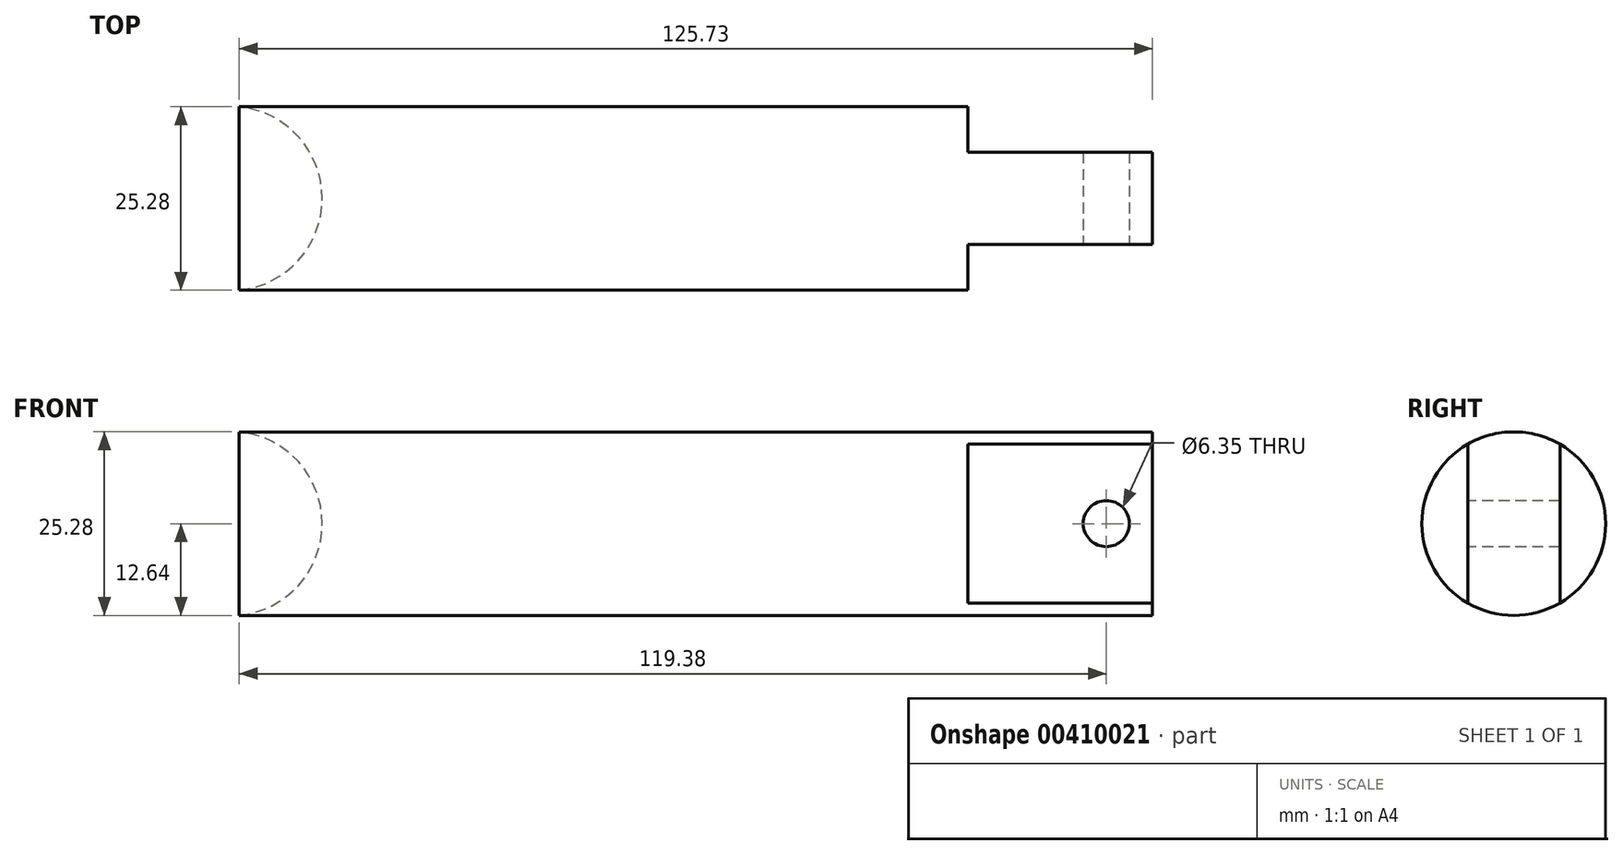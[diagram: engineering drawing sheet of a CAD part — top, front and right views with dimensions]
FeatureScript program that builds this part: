
annotation { "Feature Type Name" : "Feature", "Feature Type Description" : "" }
export const myFeature = defineFeature(function(context is Context, id is Id, definition is map)
    precondition{}
    {
        {
            var Q0;
            Q0=qCreatedBy(makeId("Front.planeOp"),FACE);
            var sketch = newSketch(context, id + "F0", { "sketchPlane" : qUnion([Q0])});
            skLineSegment(sketch, "E0", {"start": v(-84.43, 0) * mm, "end": v(77.24, 0) * mm, "construction": true});
            skLineSegment(sketch, "E1.top", {"start": v(6.35, 12.64) * mm, "end": v(133.35, 12.64) * mm});
            skLineSegment(sketch, "E1.left", {"start": v(6.35, 0) * mm, "end": v(6.35, 12.64) * mm});
            skLineSegment(sketch, "E2.right", {"start": v(133.35, 12.64) * mm, "end": v(133.35, 0) * mm});
            skLineSegment(sketch, "E3", {"start": v(6.35, 0) * mm, "end": v(133.35, 0) * mm});
            skLineSegment(sketch, "E4", {"start": v(107.95, 29.1) * mm, "end": v(107.95, -26.98) * mm, "construction": true});
            skSolve(sketch);
        }
        {
            var Q0;
            Q0 = qSketchRegion(id + "F0", true);
            var Q1;
            Q1=sQuery(id+"F0.wireOp",EDGE,"E0");
            revolve(context, id + "F1", {"entities" : qUnion([Q0]), "axis" : qUnion([Q1]), "revolveType" : RevolveType.FULL});
        }
        {
            var Q0;
            Q0=makeQuery(id+"F1.opRevolve","SWEPT_FACE",FACE,{"disambiguationData":[OSD([sQuery(id+"F0.wireOp",EDGE,"E2.right")])]});
            var sketch = newSketch(context, id + "F2", { "sketchPlane" : qUnion([Q0])});
            skLineSegment(sketch, "E5", {"start": v(0, 18.4) * mm, "end": v(0, -25.4) * mm, "construction": true});
            skLineSegment(sketch, "E6.0", {"start": v(6.35, 11) * mm, "end": v(6.35, -11) * mm});
            skLineSegment(sketch, "E7.0", {"start": v(-6.35, 11) * mm, "end": v(-6.35, -11) * mm});
            skArc(sketch, "E8", {"start": v(-6.35, 11) * mm, "mid": v(-12.7, 0) * mm, "end": v(-6.35, -11) * mm});
            skArc(sketch, "E9.trimOffspring", {"start": v(6.35, -11) * mm, "mid": v(12.7, 0) * mm, "end": v(6.35, 11) * mm});
            skSolve(sketch);
        }
        {
            var Q0;
            Q0 = qSketchRegion(id + "F2", true);
            extrude(context, id + "F3", {"entities" : qUnion([Q0]), "operationType" : NewBodyOperationType.REMOVE, "oppositeDirection" : true, "depth" : 25.4 * mm});
        }
        {
            var Q0;
            Q0=qCreatedBy(makeId("Front.planeOp"),FACE);
            var sketch = newSketch(context, id + "F4", { "sketchPlane" : qUnion([Q0])});
            skLineSegment(sketch, "E10", {"start": v(-8.82, 0) * mm, "end": v(141.34, 0) * mm, "construction": true});
            skLineSegment(sketch, "E11", {"start": v(127, 28.66) * mm, "end": v(127, -29.97) * mm, "construction": true});
            skCircle(sketch, "E12", {"center": v(127, 0) * mm, "radius": 3.18 * mm});
            skSolve(sketch);
        }
        {
            var Q0;
            Q0 = qSketchRegion(id + "F4", true);
            extrude(context, id + "F5", {"entities" : qUnion([Q0]), "operationType" : NewBodyOperationType.REMOVE, "endBound" : BoundingType.SYMMETRIC, "oppositeDirection" : true, "depth" : 25.4 * mm});
        }
        {
            var Q0;
            Q0=makeQuery(id+"F1.opRevolve","SWEPT_FACE",FACE,{"disambiguationData":[OSD([sQuery(id+"F0.wireOp",EDGE,"E1.left")])]});
            var sketch = newSketch(context, id + "F6", { "sketchPlane" : qUnion([Q0])});
            skLineSegment(sketch, "E13", {"start": v(0, 30.2) * mm, "end": v(0, -38.33) * mm, "construction": true});
            skArc(sketch, "E14", {"start": v(0, -12.7) * mm, "mid": v(12.7, 0) * mm, "end": v(0, 12.7) * mm});
            skLineSegment(sketch, "E15", {"start": v(0, 12.7) * mm, "end": v(0, -12.7) * mm});
            skSolve(sketch);
        }
        {
            var Q0;
            Q0 = qSketchRegion(id + "F6", true);
            var Q1;
            Q1=sQuery(id+"F6.wireOp",EDGE,"E13");
            revolve(context, id + "F7", {"operationType" : NewBodyOperationType.REMOVE, "entities" : qUnion([Q0]), "axis" : qUnion([Q1]), "revolveType" : RevolveType.FULL});
        }
    });
